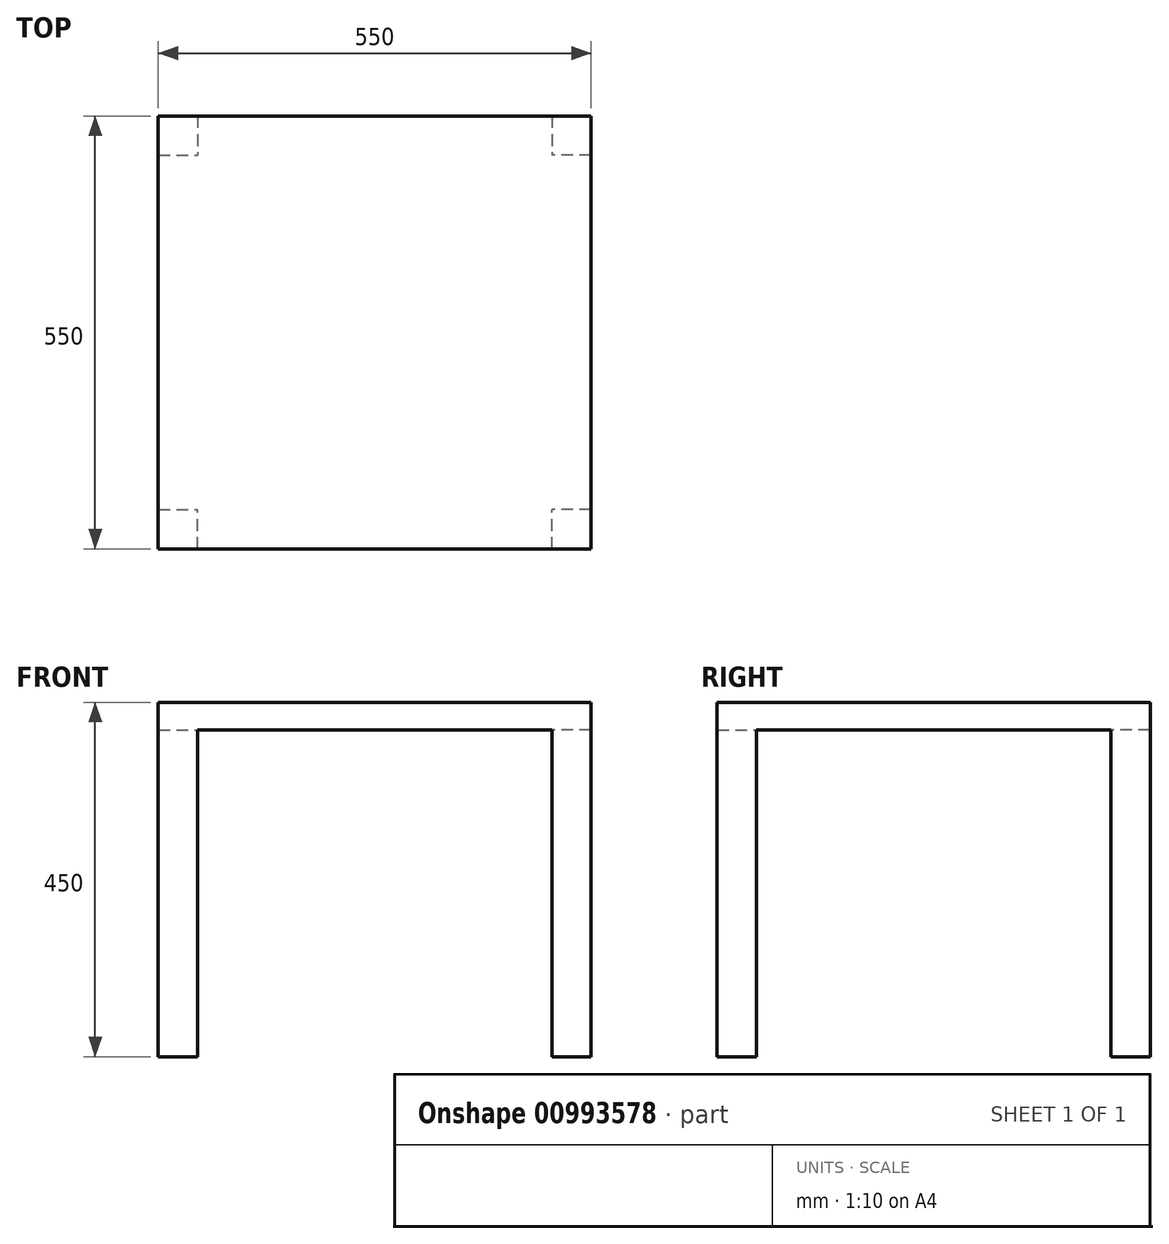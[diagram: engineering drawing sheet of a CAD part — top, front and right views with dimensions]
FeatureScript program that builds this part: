
annotation { "Feature Type Name" : "Feature", "Feature Type Description" : "" }
export const myFeature = defineFeature(function(context is Context, id is Id, definition is map)
    precondition{}
    {
        {
            var Q0;
            Q0=qCreatedBy(makeId("Top.planeOp"),FACE);
            var sketch = newSketch(context, id + "F0", { "sketchPlane" : qUnion([Q0])});
            skLineSegment(sketch, "E0.bottom", {"start": v(275, 275) * mm, "end": v(-275, 275) * mm});
            skLineSegment(sketch, "E0.top", {"start": v(275, -275) * mm, "end": v(-275, -275) * mm});
            skLineSegment(sketch, "E0.left", {"start": v(275, 275) * mm, "end": v(275, -275) * mm});
            skLineSegment(sketch, "E0.right", {"start": v(-275, 275) * mm, "end": v(-275, -275) * mm});
            skPoint(sketch, "E0.middle", {"position": v(0, 0) * mm});
            skSolve(sketch);
        }
        {
            var Q0;
            Q0 = qSketchRegion(id + "F0", true);
            extrude(context, id + "F1", {"entities" : qUnion([Q0]), "oppositeDirection" : true, "depth" : 35 * mm, "offsetDistance" : 25 * mm});
        }
        {
            var Q0;
            Q0=qCreatedBy(makeId("Top.planeOp"),FACE);
            var sketch = newSketch(context, id + "F2", { "sketchPlane" : qUnion([Q0])});
            skLineSegment(sketch, "E1.bottom", {"start": v(275, 275) * mm, "end": v(225, 275) * mm});
            skLineSegment(sketch, "E1.top", {"start": v(275, 225) * mm, "end": v(225, 225) * mm});
            skLineSegment(sketch, "E1.left", {"start": v(275, 275) * mm, "end": v(275, 225) * mm});
            skLineSegment(sketch, "E1.right", {"start": v(225, 275) * mm, "end": v(225, 225) * mm});
            skLineSegment(sketch, "E2.MirrorCS", {"start": v(275, -275) * mm, "end": v(275, -225) * mm});
            skLineSegment(sketch, "E3.MirrorCS", {"start": v(275, -275) * mm, "end": v(225, -275) * mm});
            skLineSegment(sketch, "E4.MirrorCS", {"start": v(275, -225) * mm, "end": v(225, -225) * mm});
            skLineSegment(sketch, "E5.MirrorCS", {"start": v(225, -275) * mm, "end": v(225, -225) * mm});
            skLineSegment(sketch, "E6.MirrorCS", {"start": v(-275, 275) * mm, "end": v(-275, 225) * mm});
            skLineSegment(sketch, "E7.MirrorCS", {"start": v(-275, -275) * mm, "end": v(-225, -275) * mm});
            skLineSegment(sketch, "E8.MirrorCS", {"start": v(-275, 225) * mm, "end": v(-225, 225) * mm});
            skLineSegment(sketch, "E9.MirrorCS", {"start": v(-225, -275) * mm, "end": v(-225, -225) * mm});
            skLineSegment(sketch, "E10.MirrorCS", {"start": v(-275, -275) * mm, "end": v(-275, -225) * mm});
            skLineSegment(sketch, "E11.MirrorCS", {"start": v(-275, 275) * mm, "end": v(-225, 275) * mm});
            skLineSegment(sketch, "E12.MirrorCS", {"start": v(-225, 275) * mm, "end": v(-225, 225) * mm});
            skLineSegment(sketch, "E13.MirrorCS", {"start": v(-275, -225) * mm, "end": v(-225, -225) * mm});
            skSolve(sketch);
        }
        {
            var Q0;
            Q0 = qSketchRegion(id + "F2", true);
            extrude(context, id + "F3", {"entities" : qUnion([Q0]), "operationType" : NewBodyOperationType.ADD, "oppositeDirection" : true, "depth" : 450 * mm, "offsetDistance" : 25 * mm});
        }
    });
